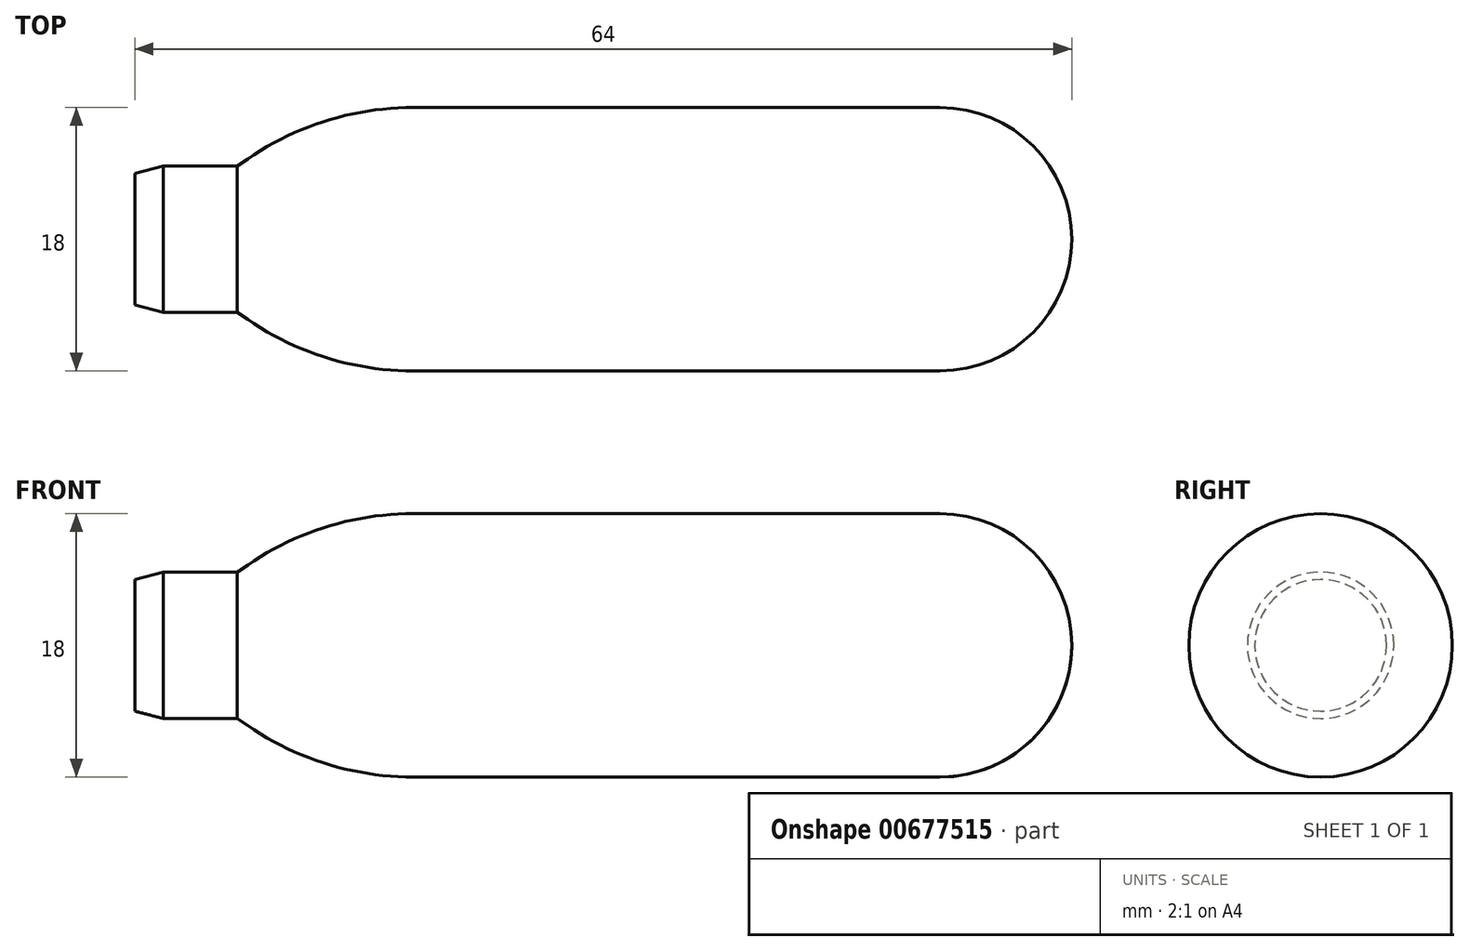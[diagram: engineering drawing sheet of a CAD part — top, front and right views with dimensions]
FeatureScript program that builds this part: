
annotation { "Feature Type Name" : "Feature", "Feature Type Description" : "" }
export const myFeature = defineFeature(function(context is Context, id is Id, definition is map)
    precondition{}
    {
        {
            var Q0;
            Q0=qCreatedBy(makeId("Front.planeOp"),FACE);
            var sketch = newSketch(context, id + "F0", { "sketchPlane" : qUnion([Q0])});
            skLineSegment(sketch, "E0", {"start": v(0, 0) * mm, "end": v(-64, 0) * mm});
            skLineSegment(sketch, "E1", {"start": v(-64, 0) * mm, "end": v(-64, 4.5) * mm});
            skLineSegment(sketch, "E2", {"start": v(-64, 4.5) * mm, "end": v(-62.06, 5) * mm});
            skLineSegment(sketch, "E3", {"start": v(0, 0) * mm, "end": v(0, 9) * mm});
            skLineSegment(sketch, "E4", {"start": v(0, 9) * mm, "end": v(-44.97, 9) * mm});
            skLineSegment(sketch, "E5", {"start": v(-62.06, 5) * mm, "end": v(-57, 5) * mm});
            skLineSegment(sketch, "E6", {"start": v(-57, 5) * mm, "end": v(-56.3, 5.49) * mm});
            skPoint(sketch, "E7.visualSharp", {"position": v(-51.18, 9) * mm});
            skArc(sketch, "E7.filletArc", {"start": v(-44.97, 9) * mm, "mid": v(-50.9, 8.1) * mm, "end": v(-56.3, 5.49) * mm});
            skSolve(sketch);
        }
        {
            var Q0;
            Q0=makeQuery(id+"F0.imprint","IMPRINT",FACE,{"disambiguationData":[TD([[makeQuery(id+"F0.imprint","IMPRINT",EDGE,{"derivedFrom":sQuery(id+"F0.wireOp",EDGE,"E0")}),-1.0]])]});
            var Q1;
            Q1=sQuery(id+"F0.wireOp",EDGE,"E0");
            revolve(context, id + "F1", {"entities" : qUnion([Q0]), "axis" : qUnion([Q1]), "revolveType" : RevolveType.FULL});
        }
        {
            var Q0;
            Q0=makeQuery(id+"F1.opRevolve","SWEPT_FACE",FACE,{"disambiguationData":[OSD([sQuery(id+"F0.wireOp",EDGE,"E4")])]});
            fillet(context, id + "F2", {"entities" : qUnion([Q0]), "radius" : 9 * mm, "tangentPropagation" : true, "allowEdgeOverflow" : false});
        }
    });
